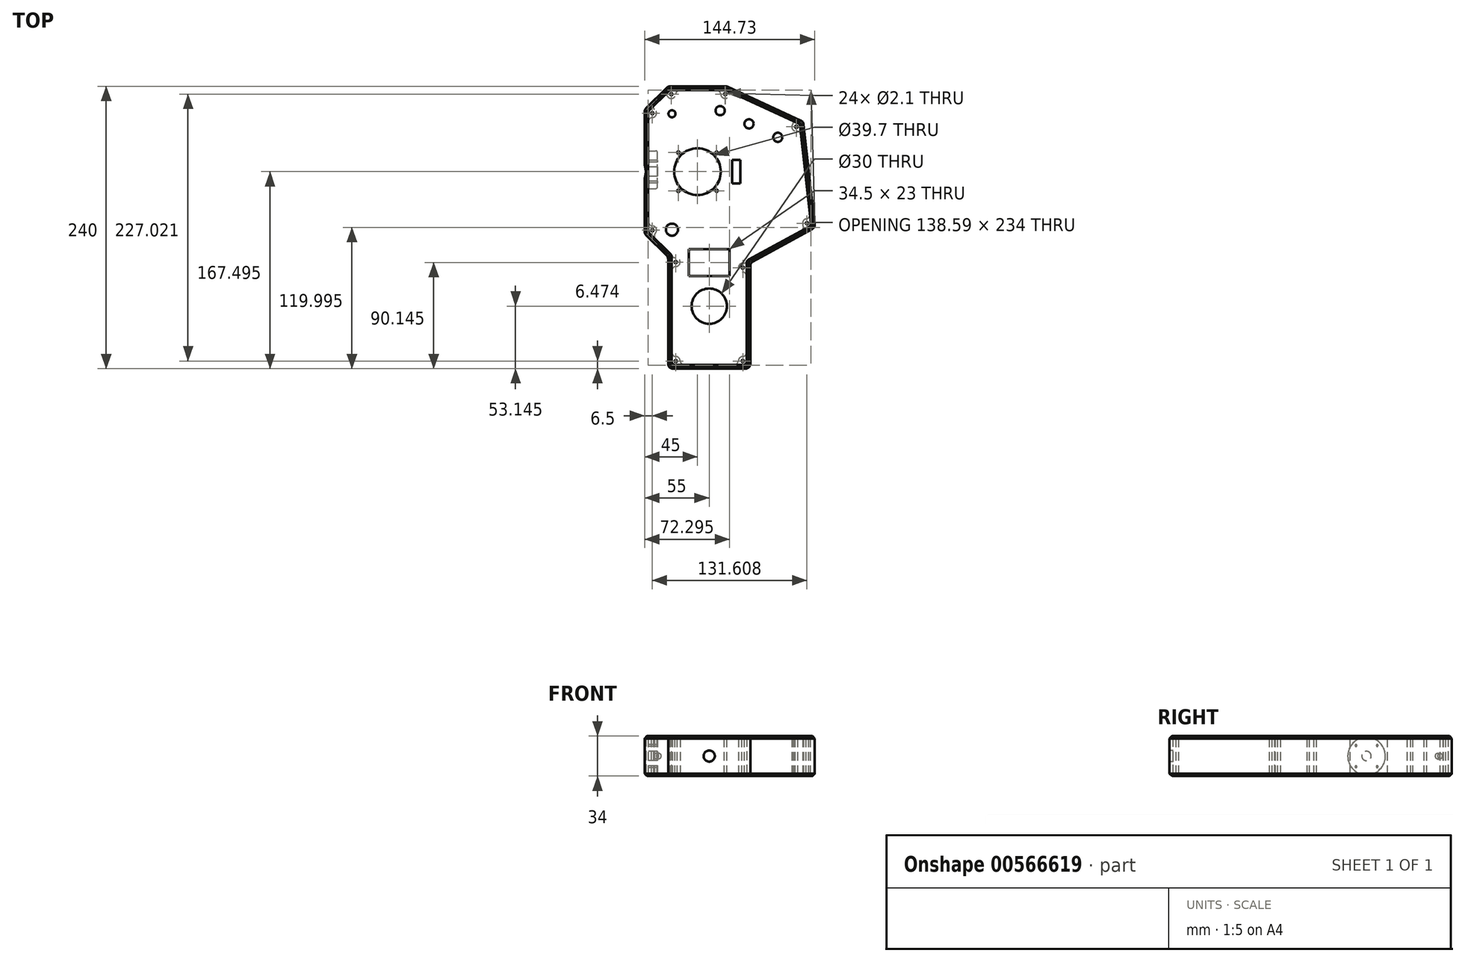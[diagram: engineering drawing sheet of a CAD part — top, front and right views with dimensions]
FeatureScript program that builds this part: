
annotation { "Feature Type Name" : "Feature", "Feature Type Description" : "" }
export const myFeature = defineFeature(function(context is Context, id is Id, definition is map)
    precondition{}
    {
        {
            var Q0;
            Q0=qCreatedBy(makeId("Top.planeOp"),FACE);
            var sketch = newSketch(context, id + "F0", { "sketchPlane" : qUnion([Q0])});
            skLineSegment(sketch, "E0", {"start": v(-64.8, 92.82) * mm, "end": v(-17.33, 92.82) * mm});
            skLineSegment(sketch, "E1", {"start": v(-15.65, 92.45) * mm, "end": v(46.5, 63.76) * mm});
            skLineSegment(sketch, "E2", {"start": v(48.8, 60.57) * mm, "end": v(58.25, -24.52) * mm});
            skLineSegment(sketch, "E3", {"start": v(56.2, -28.47) * mm, "end": v(5.63, -56.05) * mm});
            skLineSegment(sketch, "E4", {"start": v(3.55, -59.56) * mm, "end": v(3.55, -143.18) * mm});
            skLineSegment(sketch, "E5", {"start": v(-0.45, -147.18) * mm, "end": v(-62.45, -147.18) * mm});
            skLineSegment(sketch, "E6", {"start": v(-66.45, -143.18) * mm, "end": v(-66.45, -53.84) * mm});
            skLineSegment(sketch, "E7", {"start": v(-67.62, -51.01) * mm, "end": v(-85.28, -33.36) * mm});
            skLineSegment(sketch, "E8", {"start": v(-86.45, -30.53) * mm, "end": v(-86.45, 71.16) * mm});
            skLineSegment(sketch, "E9", {"start": v(-85.28, 73.99) * mm, "end": v(-67.62, 91.64) * mm});
            skLineSegment(sketch, "E10.0", {"start": v(53.58, -26.48) * mm, "end": v(2.11, -54.55) * mm});
            skLineSegment(sketch, "E10.1", {"start": v(45.94, 59.12) * mm, "end": v(55.12, -23.51) * mm});
            skLineSegment(sketch, "E10.2", {"start": v(0.55, -57.18) * mm, "end": v(0.55, -141.18) * mm});
            skLineSegment(sketch, "E10.3", {"start": v(-16.51, 89.54) * mm, "end": v(44.22, 61.51) * mm});
            skLineSegment(sketch, "E10.4", {"start": v(-63.96, 89.82) * mm, "end": v(-17.77, 89.82) * mm});
            skLineSegment(sketch, "E10.5", {"start": v(-82.57, 72.45) * mm, "end": v(-66.09, 88.94) * mm});
            skLineSegment(sketch, "E10.6", {"start": v(-2.45, -144.18) * mm, "end": v(-60.45, -144.18) * mm});
            skLineSegment(sketch, "E10.7", {"start": v(-63.45, -141.18) * mm, "end": v(-63.45, -52.18) * mm});
            skLineSegment(sketch, "E10.8", {"start": v(-64.33, -50.06) * mm, "end": v(-82.57, -31.82) * mm});
            skLineSegment(sketch, "E10.9", {"start": v(-83.45, -29.7) * mm, "end": v(-83.45, 70.33) * mm});
            skPoint(sketch, "E11.visualSharp", {"position": v(-66.45, 92.82) * mm});
            skArc(sketch, "E11.filletArc", {"start": v(-64.8, 92.82) * mm, "mid": v(-66.32, 92.51) * mm, "end": v(-67.62, 91.64) * mm});
            skPoint(sketch, "E12.visualSharp", {"position": v(-16.45, 92.82) * mm});
            skArc(sketch, "E12.filletArc", {"start": v(-15.65, 92.45) * mm, "mid": v(-16.47, 92.72) * mm, "end": v(-17.33, 92.82) * mm});
            skPoint(sketch, "E13.visualSharp", {"position": v(48.55, 62.82) * mm});
            skArc(sketch, "E13.filletArc", {"start": v(48.8, 60.57) * mm, "mid": v(48.07, 62.47) * mm, "end": v(46.5, 63.76) * mm});
            skPoint(sketch, "E14.visualSharp", {"position": v(58.55, -27.18) * mm});
            skArc(sketch, "E14.filletArc", {"start": v(56.2, -28.47) * mm, "mid": v(57.83, -26.8) * mm, "end": v(58.25, -24.52) * mm});
            skPoint(sketch, "E15.visualSharp", {"position": v(3.55, -57.18) * mm});
            skArc(sketch, "E15.filletArc", {"start": v(5.63, -56.05) * mm, "mid": v(4.11, -57.52) * mm, "end": v(3.55, -59.56) * mm});
            skPoint(sketch, "E16.visualSharp", {"position": v(3.55, -147.18) * mm});
            skArc(sketch, "E16.filletArc", {"start": v(-0.45, -147.18) * mm, "mid": v(2.38, -146.01) * mm, "end": v(3.55, -143.18) * mm});
            skPoint(sketch, "E17.visualSharp", {"position": v(-66.45, -147.18) * mm});
            skArc(sketch, "E17.filletArc", {"start": v(-66.45, -143.18) * mm, "mid": v(-65.28, -146.01) * mm, "end": v(-62.45, -147.18) * mm});
            skPoint(sketch, "E18.visualSharp", {"position": v(-66.45, -52.18) * mm});
            skArc(sketch, "E18.filletArc", {"start": v(-66.45, -53.84) * mm, "mid": v(-66.75, -52.31) * mm, "end": v(-67.62, -51.01) * mm});
            skPoint(sketch, "E19.visualSharp", {"position": v(-86.45, -32.18) * mm});
            skArc(sketch, "E19.filletArc", {"start": v(-86.45, -30.53) * mm, "mid": v(-86.15, -32.06) * mm, "end": v(-85.28, -33.36) * mm});
            skPoint(sketch, "E20.visualSharp", {"position": v(-86.45, 72.82) * mm});
            skArc(sketch, "E20.filletArc", {"start": v(-85.28, 73.99) * mm, "mid": v(-86.15, 72.69) * mm, "end": v(-86.45, 71.16) * mm});
            skPoint(sketch, "E21.visualSharp", {"position": v(-83.45, -30.94) * mm});
            skArc(sketch, "E21.filletArc", {"start": v(-83.45, -29.7) * mm, "mid": v(-83.22, -30.85) * mm, "end": v(-82.57, -31.82) * mm});
            skPoint(sketch, "E22.visualSharp", {"position": v(-83.45, 71.57) * mm});
            skArc(sketch, "E22.filletArc", {"start": v(-82.57, 72.45) * mm, "mid": v(-83.22, 71.48) * mm, "end": v(-83.45, 70.33) * mm});
            skPoint(sketch, "E23.visualSharp", {"position": v(-65.2, 89.82) * mm});
            skArc(sketch, "E23.filletArc", {"start": v(-63.96, 89.82) * mm, "mid": v(-65.11, 89.59) * mm, "end": v(-66.09, 88.94) * mm});
            skPoint(sketch, "E24.visualSharp", {"position": v(-17.1, 89.82) * mm});
            skArc(sketch, "E24.filletArc", {"start": v(-16.51, 89.54) * mm, "mid": v(-17.12, 89.75) * mm, "end": v(-17.77, 89.82) * mm});
            skPoint(sketch, "E25.visualSharp", {"position": v(-63.45, -50.94) * mm});
            skArc(sketch, "E25.filletArc", {"start": v(-63.45, -52.18) * mm, "mid": v(-63.68, -51.04) * mm, "end": v(-64.33, -50.06) * mm});
            skPoint(sketch, "E26.visualSharp", {"position": v(0.55, -55.4) * mm});
            skArc(sketch, "E26.filletArc", {"start": v(2.11, -54.55) * mm, "mid": v(0.97, -55.65) * mm, "end": v(0.55, -57.18) * mm});
            skPoint(sketch, "E27.visualSharp", {"position": v(55.35, -25.52) * mm});
            skArc(sketch, "E27.filletArc", {"start": v(53.58, -26.48) * mm, "mid": v(54.8, -25.23) * mm, "end": v(55.12, -23.51) * mm});
            skPoint(sketch, "E28.visualSharp", {"position": v(45.76, 60.8) * mm});
            skArc(sketch, "E28.filletArc", {"start": v(45.94, 59.12) * mm, "mid": v(45.4, 60.54) * mm, "end": v(44.22, 61.51) * mm});
            skPoint(sketch, "E29.visualSharp", {"position": v(0.55, -144.18) * mm});
            skArc(sketch, "E29.filletArc", {"start": v(-2.45, -144.18) * mm, "mid": v(-0.33, -143.3) * mm, "end": v(0.55, -141.18) * mm});
            skPoint(sketch, "E30.visualSharp", {"position": v(-63.45, -144.18) * mm});
            skArc(sketch, "E30.filletArc", {"start": v(-63.45, -141.18) * mm, "mid": v(-62.57, -143.3) * mm, "end": v(-60.45, -144.18) * mm});
            skSolve(sketch);
        }
        {
            var Q0;
            Q0=makeQuery(id+"F0.imprint","IMPRINT",FACE,{"disambiguationData":[TD([[makeQuery(id+"F0.imprint","IMPRINT",EDGE,{"derivedFrom":sQuery(id+"F0.wireOp",EDGE,"E0")}),-1.0]])]});
            extrude(context, id + "F1", {"entities" : qUnion([Q0]), "endBound" : BoundingType.SYMMETRIC, "depth" : 34 * mm, "offsetDistance" : 25 * mm});
        }
        {
            var Q0;
            Q0=qCreatedBy(makeId("Top.planeOp"),FACE);
            var sketch = newSketch(context, id + "F2", { "sketchPlane" : qUnion([Q0])});
            skLineSegment(sketch, "E31.0", {"start": v(-84.95, -31.56) * mm, "end": v(-84.95, 72.2) * mm, "construction": true});
            skLineSegment(sketch, "E31.1", {"start": v(-64.95, -51.56) * mm, "end": v(-84.95, -31.56) * mm, "construction": true});
            skLineSegment(sketch, "E31.2", {"start": v(-84.95, 72.2) * mm, "end": v(-65.83, 91.32) * mm, "construction": true});
            skLineSegment(sketch, "E31.3", {"start": v(-64.95, -145.68) * mm, "end": v(-64.95, -51.56) * mm, "construction": true});
            skLineSegment(sketch, "E31.4", {"start": v(2.05, -145.68) * mm, "end": v(-64.95, -145.68) * mm, "construction": true});
            skLineSegment(sketch, "E31.5", {"start": v(2.05, -56.3) * mm, "end": v(2.05, -145.68) * mm, "construction": true});
            skLineSegment(sketch, "E31.6", {"start": v(-65.83, 91.32) * mm, "end": v(-16.78, 91.32) * mm, "construction": true});
            skLineSegment(sketch, "E31.7", {"start": v(-16.78, 91.32) * mm, "end": v(47.15, 61.8) * mm, "construction": true});
            skLineSegment(sketch, "E31.8", {"start": v(47.15, 61.8) * mm, "end": v(56.95, -26.35) * mm, "construction": true});
            skLineSegment(sketch, "E31.9", {"start": v(56.95, -26.35) * mm, "end": v(2.05, -56.3) * mm, "construction": true});
            skSolve(sketch);
        }
        {
            var Q0;
            Q0=qCreatedBy(makeId("Top.planeOp"),FACE);
            var sketch = newSketch(context, id + "F3", { "sketchPlane" : qUnion([Q0])});
            skCircle(sketch, "E32", {"center": v(-79.95, 70.12) * mm, "radius": 3.75 * mm});
            skCircle(sketch, "E33", {"center": v(-79.95, 70.12) * mm, "radius": 1.05 * mm});
            skCircle(sketch, "E34", {"center": v(-63.76, 86.32) * mm, "radius": 3.75 * mm});
            skCircle(sketch, "E35", {"center": v(-63.76, 86.32) * mm, "radius": 1.05 * mm});
            skCircle(sketch, "E36", {"center": v(-17.88, 86.32) * mm, "radius": 3.75 * mm});
            skCircle(sketch, "E37", {"center": v(-17.88, 86.32) * mm, "radius": 1.05 * mm});
            skCircle(sketch, "E38", {"center": v(42.5, 58.45) * mm, "radius": 3.75 * mm});
            skCircle(sketch, "E39", {"center": v(42.5, 58.45) * mm, "radius": 1.05 * mm});
            skCircle(sketch, "E40", {"center": v(51.6, -23.57) * mm, "radius": 3.75 * mm});
            skCircle(sketch, "E41", {"center": v(51.6, -23.57) * mm, "radius": 1.05 * mm});
            skCircle(sketch, "E42", {"center": v(-2.95, -140.68) * mm, "radius": 3.75 * mm});
            skCircle(sketch, "E43", {"center": v(-2.95, -140.68) * mm, "radius": 1.05 * mm});
            skCircle(sketch, "E44", {"center": v(-59.95, -140.68) * mm, "radius": 3.75 * mm});
            skCircle(sketch, "E45", {"center": v(-59.95, -140.68) * mm, "radius": 1.05 * mm});
            skCircle(sketch, "E46", {"center": v(-79.95, -29.5) * mm, "radius": 3.75 * mm});
            skCircle(sketch, "E47", {"center": v(-79.95, -29.5) * mm, "radius": 1.05 * mm});
            skCircle(sketch, "E48", {"center": v(-59.95, -56.56) * mm, "radius": 3.75 * mm});
            skCircle(sketch, "E49", {"center": v(-59.95, -56.56) * mm, "radius": 1.05 * mm});
            skCircle(sketch, "E50", {"center": v(-2.95, -61.3) * mm, "radius": 3.75 * mm});
            skCircle(sketch, "E51", {"center": v(-2.95, -61.3) * mm, "radius": 1.05 * mm});
            skLineSegment(sketch, "E52.bottom", {"start": v(-83.45, 5.97) * mm, "end": v(-75.45, 5.97) * mm});
            skLineSegment(sketch, "E52.top", {"start": v(-83.45, 37.97) * mm, "end": v(-75.45, 37.97) * mm});
            skLineSegment(sketch, "E52.left", {"start": v(-83.45, 5.97) * mm, "end": v(-83.45, 37.97) * mm});
            skLineSegment(sketch, "E52.right", {"start": v(-75.45, 5.97) * mm, "end": v(-75.45, 37.97) * mm});
            skSolve(sketch);
        }
        {
            var Q0;
            Q0=makeQuery(id+"F3.imprint","IMPRINT",FACE,{"disambiguationData":[TD([[makeQuery(id+"F3.imprint","IMPRINT",EDGE,{"derivedFrom":sQuery(id+"F3.wireOp",EDGE,"E44")}),1.0]])]});
            var Q1;
            Q1=makeQuery(id+"F3.imprint","IMPRINT",FACE,{"disambiguationData":[TD([[makeQuery(id+"F3.imprint","IMPRINT",EDGE,{"derivedFrom":sQuery(id+"F3.wireOp",EDGE,"E42")}),1.0]])]});
            var Q2;
            Q2=makeQuery(id+"F3.imprint","IMPRINT",FACE,{"disambiguationData":[TD([[makeQuery(id+"F3.imprint","IMPRINT",EDGE,{"derivedFrom":sQuery(id+"F3.wireOp",EDGE,"E50")}),1.0]])]});
            var Q3;
            Q3=makeQuery(id+"F3.imprint","IMPRINT",FACE,{"disambiguationData":[TD([[makeQuery(id+"F3.imprint","IMPRINT",EDGE,{"derivedFrom":sQuery(id+"F3.wireOp",EDGE,"E48")}),1.0]])]});
            var Q4;
            Q4=makeQuery(id+"F3.imprint","IMPRINT",FACE,{"disambiguationData":[TD([[makeQuery(id+"F3.imprint","IMPRINT",EDGE,{"derivedFrom":sQuery(id+"F3.wireOp",EDGE,"E46")}),1.0]])]});
            var Q5;
            Q5=makeQuery(id+"F3.imprint","IMPRINT",FACE,{"disambiguationData":[TD([[makeQuery(id+"F3.imprint","IMPRINT",EDGE,{"derivedFrom":sQuery(id+"F3.wireOp",EDGE,"E40")}),1.0]])]});
            var Q6;
            Q6=makeQuery(id+"F3.imprint","IMPRINT",FACE,{"disambiguationData":[TD([[makeQuery(id+"F3.imprint","IMPRINT",EDGE,{"derivedFrom":sQuery(id+"F3.wireOp",EDGE,"E38")}),1.0]])]});
            var Q7;
            Q7=makeQuery(id+"F3.imprint","IMPRINT",FACE,{"disambiguationData":[TD([[makeQuery(id+"F3.imprint","IMPRINT",EDGE,{"derivedFrom":sQuery(id+"F3.wireOp",EDGE,"E36")}),1.0]])]});
            var Q8;
            Q8=makeQuery(id+"F3.imprint","IMPRINT",FACE,{"disambiguationData":[TD([[makeQuery(id+"F3.imprint","IMPRINT",EDGE,{"derivedFrom":sQuery(id+"F3.wireOp",EDGE,"E34")}),1.0]])]});
            var Q9;
            Q9=makeQuery(id+"F3.imprint","IMPRINT",FACE,{"disambiguationData":[TD([[makeQuery(id+"F3.imprint","IMPRINT",EDGE,{"derivedFrom":sQuery(id+"F3.wireOp",EDGE,"E32")}),1.0]])]});
            var Q10;
            Q10=makeQuery(id+"F3.imprint","IMPRINT",FACE,{"disambiguationData":[TD([[makeQuery(id+"F3.imprint","IMPRINT",EDGE,{"derivedFrom":sQuery(id+"F3.wireOp",EDGE,"E52.bottom")}),1.0]])]});
            extrude(context, id + "F4", {"entities" : qUnion([Q0, Q1, Q2, Q3, Q4, Q5, Q6, Q7, Q8, Q9, Q10]), "operationType" : NewBodyOperationType.ADD, "endBound" : BoundingType.SYMMETRIC, "depth" : 30 * mm, "offsetDistance" : 25 * mm});
        }
        {
            var Q0;
            Q0=makeQuery(id+"F4.boolean.opBoolean","INTERSECT",EDGE,{"disambiguationData":[OD(0.0)],"derivedFrom":[makeQuery(id+"F1.opExtrude","SWEPT_FACE",FACE,{"disambiguationData":[OSD([sQuery(id+"F0.wireOp",EDGE,"E10.7")])]}),makeQuery(id+"F4.opExtrude","SWEPT_FACE",FACE,{"disambiguationData":[OSD([sQuery(id+"F3.wireOp",EDGE,"E48")])]})]});
            var Q1;
            Q1=makeQuery(id+"F4.boolean.opBoolean","INTERSECT",EDGE,{"disambiguationData":[OD(1.0)],"derivedFrom":[makeQuery(id+"F1.opExtrude","SWEPT_FACE",FACE,{"disambiguationData":[OSD([sQuery(id+"F0.wireOp",EDGE,"E10.7")])]}),makeQuery(id+"F4.opExtrude","SWEPT_FACE",FACE,{"disambiguationData":[OSD([sQuery(id+"F3.wireOp",EDGE,"E48")])]})]});
            var Q2;
            Q2=makeQuery(id+"F4.boolean.opBoolean","INTERSECT",EDGE,{"derivedFrom":[makeQuery(id+"F1.opExtrude","SWEPT_FACE",FACE,{"disambiguationData":[OSD([sQuery(id+"F0.wireOp",EDGE,"E10.9")])]}),makeQuery(id+"F4.opExtrude","SWEPT_FACE",FACE,{"disambiguationData":[OSD([sQuery(id+"F3.wireOp",EDGE,"E32")])]})]});
            var Q3;
            Q3=makeQuery(id+"F4.boolean.opBoolean","INTERSECT",EDGE,{"derivedFrom":[makeQuery(id+"F1.opExtrude","SWEPT_FACE",FACE,{"disambiguationData":[OSD([sQuery(id+"F0.wireOp",EDGE,"E10.4")])]}),makeQuery(id+"F4.opExtrude","SWEPT_FACE",FACE,{"disambiguationData":[OSD([sQuery(id+"F3.wireOp",EDGE,"E36")])]})]});
            var Q4;
            Q4=makeQuery(id+"F4.boolean.opBoolean","INTERSECT",EDGE,{"derivedFrom":[makeQuery(id+"F1.opExtrude","SWEPT_FACE",FACE,{"disambiguationData":[OSD([sQuery(id+"F0.wireOp",EDGE,"E10.4")])]}),makeQuery(id+"F4.opExtrude","SWEPT_FACE",FACE,{"disambiguationData":[OSD([sQuery(id+"F3.wireOp",EDGE,"E34")])]})]});
            var Q5;
            Q5=makeQuery(id+"F4.boolean.opBoolean","INTERSECT",EDGE,{"derivedFrom":[makeQuery(id+"F1.opExtrude","SWEPT_FACE",FACE,{"disambiguationData":[OSD([sQuery(id+"F0.wireOp",EDGE,"E10.1")])]}),makeQuery(id+"F4.opExtrude","SWEPT_FACE",FACE,{"disambiguationData":[OSD([sQuery(id+"F3.wireOp",EDGE,"E38")])]})]});
            var Q6;
            Q6=makeQuery(id+"F4.boolean.opBoolean","INTERSECT",EDGE,{"derivedFrom":[makeQuery(id+"F1.opExtrude","SWEPT_FACE",FACE,{"disambiguationData":[OSD([sQuery(id+"F0.wireOp",EDGE,"E10.0")])]}),makeQuery(id+"F4.opExtrude","SWEPT_FACE",FACE,{"disambiguationData":[OSD([sQuery(id+"F3.wireOp",EDGE,"E40")])]})]});
            var Q7;
            Q7=makeQuery(id+"F4.boolean.opBoolean","INTERSECT",EDGE,{"derivedFrom":[makeQuery(id+"F1.opExtrude","SWEPT_FACE",FACE,{"disambiguationData":[OSD([sQuery(id+"F0.wireOp",EDGE,"E10.1")])]}),makeQuery(id+"F4.opExtrude","SWEPT_FACE",FACE,{"disambiguationData":[OSD([sQuery(id+"F3.wireOp",EDGE,"E40")])]})]});
            var Q8;
            Q8=makeQuery(id+"F4.boolean.opBoolean","INTERSECT",EDGE,{"derivedFrom":[makeQuery(id+"F1.opExtrude","SWEPT_FACE",FACE,{"disambiguationData":[OSD([sQuery(id+"F0.wireOp",EDGE,"E10.8")])]}),makeQuery(id+"F4.opExtrude","SWEPT_FACE",FACE,{"disambiguationData":[OSD([sQuery(id+"F3.wireOp",EDGE,"E46")])]})]});
            var Q9;
            Q9=makeQuery(id+"F4.boolean.opBoolean","INTERSECT",EDGE,{"derivedFrom":[makeQuery(id+"F1.opExtrude","SWEPT_FACE",FACE,{"disambiguationData":[OSD([sQuery(id+"F0.wireOp",EDGE,"E10.9")])]}),makeQuery(id+"F4.opExtrude","SWEPT_FACE",FACE,{"disambiguationData":[OSD([sQuery(id+"F3.wireOp",EDGE,"E46")])]})]});
            var Q10;
            Q10=makeQuery(id+"F4.boolean.opBoolean","INTERSECT",EDGE,{"derivedFrom":[makeQuery(id+"F1.opExtrude","SWEPT_FACE",FACE,{"disambiguationData":[OSD([sQuery(id+"F0.wireOp",EDGE,"E10.7")])]}),makeQuery(id+"F4.opExtrude","SWEPT_FACE",FACE,{"disambiguationData":[OSD([sQuery(id+"F3.wireOp",EDGE,"E44")])]})]});
            var Q11;
            Q11=makeQuery(id+"F4.boolean.opBoolean","INTERSECT",EDGE,{"derivedFrom":[makeQuery(id+"F1.opExtrude","SWEPT_FACE",FACE,{"disambiguationData":[OSD([sQuery(id+"F0.wireOp",EDGE,"E10.6")])]}),makeQuery(id+"F4.opExtrude","SWEPT_FACE",FACE,{"disambiguationData":[OSD([sQuery(id+"F3.wireOp",EDGE,"E44")])]})]});
            var Q12;
            Q12=makeQuery(id+"F4.boolean.opBoolean","INTERSECT",EDGE,{"derivedFrom":[makeQuery(id+"F1.opExtrude","SWEPT_FACE",FACE,{"disambiguationData":[OSD([sQuery(id+"F0.wireOp",EDGE,"E10.6")])]}),makeQuery(id+"F4.opExtrude","SWEPT_FACE",FACE,{"disambiguationData":[OSD([sQuery(id+"F3.wireOp",EDGE,"E42")])]})]});
            var Q13;
            Q13=makeQuery(id+"F4.boolean.opBoolean","INTERSECT",EDGE,{"derivedFrom":[makeQuery(id+"F1.opExtrude","SWEPT_FACE",FACE,{"disambiguationData":[OSD([sQuery(id+"F0.wireOp",EDGE,"E10.2")])]}),makeQuery(id+"F4.opExtrude","SWEPT_FACE",FACE,{"disambiguationData":[OSD([sQuery(id+"F3.wireOp",EDGE,"E42")])]})]});
            var Q14;
            Q14=makeQuery(id+"F4.boolean.opBoolean","INTERSECT",EDGE,{"disambiguationData":[OD(0.0)],"derivedFrom":[makeQuery(id+"F1.opExtrude","SWEPT_FACE",FACE,{"disambiguationData":[OSD([sQuery(id+"F0.wireOp",EDGE,"E10.2")])]}),makeQuery(id+"F4.opExtrude","SWEPT_FACE",FACE,{"disambiguationData":[OSD([sQuery(id+"F3.wireOp",EDGE,"E50")])]})]});
            var Q15;
            Q15=makeQuery(id+"F4.boolean.opBoolean","INTERSECT",EDGE,{"disambiguationData":[OD(1.0)],"derivedFrom":[makeQuery(id+"F1.opExtrude","SWEPT_FACE",FACE,{"disambiguationData":[OSD([sQuery(id+"F0.wireOp",EDGE,"E10.2")])]}),makeQuery(id+"F4.opExtrude","SWEPT_FACE",FACE,{"disambiguationData":[OSD([sQuery(id+"F3.wireOp",EDGE,"E50")])]})]});
            var Q16;
            Q16=makeQuery(id+"F4.opExtrude","SWEPT_EDGE",EDGE,{"disambiguationData":[OSD([sQuery(id+"F3.wireOp",EDGE,"E52.bottom"),sQuery(id+"F3.wireOp",EDGE,"E52.left")])]});
            var Q17;
            Q17=makeQuery(id+"F4.opExtrude","SWEPT_EDGE",EDGE,{"disambiguationData":[OSD([sQuery(id+"F3.wireOp",EDGE,"E52.top"),sQuery(id+"F3.wireOp",EDGE,"E52.left")])]});
            fillet(context, id + "F5", {"entities" : qUnion([Q0, Q1, Q2, Q3, Q4, Q5, Q6, Q7, Q8, Q9, Q10, Q11, Q12, Q13, Q14, Q15, Q16, Q17]), "radius" : 4 * mm, "tangentPropagation" : true, "defaultsChanged" : false, "vertexSettings" : [], "allowEdgeOverflow" : false});
        }
        {
            var Q0;
            Q0=makeQuery(id+"F1.opExtrude","SWEPT_FACE",FACE,{"disambiguationData":[OSD([sQuery(id+"F0.wireOp",EDGE,"E5")])]});
            var sketch = newSketch(context, id + "F6", { "sketchPlane" : qUnion([Q0])});
            skCircle(sketch, "E53", {"center": v(-31.45, 0) * mm, "radius": 4.75 * mm});
            skSolve(sketch);
        }
        {
            var Q0;
            Q0=makeQuery(id+"F6.imprint","IMPRINT",FACE,{"disambiguationData":[TD([[makeQuery(id+"F6.imprint","IMPRINT",EDGE,{"derivedFrom":sQuery(id+"F6.wireOp",EDGE,"E53")}),1.0]])]});
            var Q1;
            Q1=makeQuery(id+"F6.imprint","IMPRINT",FACE,{"disambiguationData":[TD([[makeQuery(id+"F6.imprint","IMPRINT",EDGE,{"derivedFrom":sQuery(id+"F6.wireOp",EDGE,"O80JE7wC-Ytc9-j5uM-N2nM-kXgGOOiKGs8d")}),1.0]])]});
            extrude(context, id + "F7", {"entities" : qUnion([Q0, Q1]), "operationType" : NewBodyOperationType.REMOVE, "oppositeDirection" : true, "depth" : 3 * mm, "offsetDistance" : 25 * mm});
        }
        {
            var Q0;
            Q0=makeQuery(id+"F1.opExtrude","SWEPT_FACE",FACE,{"disambiguationData":[OSD([sQuery(id+"F0.wireOp",EDGE,"E8")])]});
            var sketch = newSketch(context, id + "F8", { "sketchPlane" : qUnion([Q0])});
            skCircle(sketch, "E54", {"center": v(-20.32, 0) * mm, "radius": 16 * mm});
            skSolve(sketch);
        }
        {
            var Q0;
            {var subQ0=sQuery(id+"F8.wireOp",EDGE,"E54");var subQ1=sQuery(id+"F0.wireOp",EDGE,"E8");var subQ2=makeQuery(id+"F1.opExtrude","CAP_EDGE",EDGE,{"disambiguationData":[OSD([subQ1])],"isStart":false});var subQ3=makeQuery(id+"F8.imprint","INTERSECT",VERTEX,{"disambiguationData":[OD(0.0)],"derivedFrom":[subQ2,subQ0]});Q0=makeQuery(id+"F8.imprint","IMPRINT",FACE,{"disambiguationData":[TD([[makeQuery(id+"F8.imprint","IMPRINT",EDGE,{"disambiguationData":[TD([[subQ3,-1.0]])],"derivedFrom":subQ0}),1.0]])]});}
            extrude(context, id + "F9", {"entities" : qUnion([Q0]), "operationType" : NewBodyOperationType.REMOVE, "oppositeDirection" : true, "depth" : 1 * mm, "offsetDistance" : 25 * mm});
        }
        {
            var Q0;
            Q0=makeQuery(id+"F9.boolean.opBoolean","COPY",FACE,{"derivedFrom":makeQuery(id+"F9.opExtrude","CAP_FACE",FACE,{"disambiguationData":[OSD([sQuery(id+"F0.wireOp",EDGE,"E8"),sQuery(id+"F8.wireOp",EDGE,"E54")])],"isStart":false})});
            var sketch = newSketch(context, id + "F10", { "sketchPlane" : qUnion([Q0])});
            skCircle(sketch, "E55", {"center": v(-20.32, 0) * mm, "radius": 4 * mm});
            skCircle(sketch, "E56", {"center": v(-29.32, 9) * mm, "radius": 0.8 * mm});
            skCircle(sketch, "E57", {"center": v(-11.32, 9) * mm, "radius": 0.8 * mm});
            skCircle(sketch, "E58", {"center": v(-11.32, -9) * mm, "radius": 0.8 * mm});
            skCircle(sketch, "E59", {"center": v(-29.32, -9) * mm, "radius": 0.8 * mm});
            skSolve(sketch);
        }
        {
            var Q0;
            Q0=makeQuery(id+"F10.imprint","IMPRINT",FACE,{"disambiguationData":[TD([[makeQuery(id+"F10.imprint","IMPRINT",EDGE,{"derivedFrom":sQuery(id+"F10.wireOp",EDGE,"E56")}),1.0]])]});
            var Q1;
            Q1=makeQuery(id+"F10.imprint","IMPRINT",FACE,{"disambiguationData":[TD([[makeQuery(id+"F10.imprint","IMPRINT",EDGE,{"derivedFrom":sQuery(id+"F10.wireOp",EDGE,"E57")}),1.0]])]});
            var Q2;
            Q2=makeQuery(id+"F10.imprint","IMPRINT",FACE,{"disambiguationData":[TD([[makeQuery(id+"F10.imprint","IMPRINT",EDGE,{"derivedFrom":sQuery(id+"F10.wireOp",EDGE,"E55")}),1.0]])]});
            var Q3;
            Q3=makeQuery(id+"F10.imprint","IMPRINT",FACE,{"disambiguationData":[TD([[makeQuery(id+"F10.imprint","IMPRINT",EDGE,{"derivedFrom":sQuery(id+"F10.wireOp",EDGE,"E58")}),1.0]])]});
            var Q4;
            Q4=makeQuery(id+"F10.imprint","IMPRINT",FACE,{"disambiguationData":[TD([[makeQuery(id+"F10.imprint","IMPRINT",EDGE,{"derivedFrom":sQuery(id+"F10.wireOp",EDGE,"E59")}),1.0]])]});
            extrude(context, id + "F11", {"entities" : qUnion([Q0, Q1, Q2, Q3, Q4]), "operationType" : NewBodyOperationType.REMOVE, "depth" : -10.9 * mm, "offsetDistance" : 25 * mm});
        }
        {
            var Q0;
            Q0=makeQuery(id+"F4.opExtrude","SWEPT_EDGE",EDGE,{"disambiguationData":[OSD([sQuery(id+"F3.wireOp",EDGE,"E52.bottom"),sQuery(id+"F3.wireOp",EDGE,"E52.right")])]});
            var Q1;
            Q1=makeQuery(id+"F4.opExtrude","SWEPT_EDGE",EDGE,{"disambiguationData":[OSD([sQuery(id+"F3.wireOp",EDGE,"E52.top"),sQuery(id+"F3.wireOp",EDGE,"E52.right")])]});
            fillet(context, id + "F12", {"entities" : qUnion([Q0, Q1]), "radius" : 1.5 * mm, "tangentPropagation" : true, "allowEdgeOverflow" : false});
        }
        {
            var Q0;
            Q0=makeQuery(id+"F1.opExtrude","SWEPT_FACE",FACE,{"disambiguationData":[OSD([sQuery(id+"F0.wireOp",EDGE,"E9")])]});
            var sketch = newSketch(context, id + "F13", { "sketchPlane" : qUnion([Q0])});
            skCircle(sketch, "E60", {"center": v(-4.5, 0) * mm, "radius": 2.5 * mm});
            skPoint(sketch, "E60.centerSnap0", {"position": v(-4.5, 17) * mm});
            skSolve(sketch);
        }
        {
            var Q0;
            Q0=makeQuery(id+"F13.imprint","IMPRINT",FACE,{"disambiguationData":[TD([[makeQuery(id+"F13.imprint","IMPRINT",EDGE,{"derivedFrom":sQuery(id+"F13.wireOp",EDGE,"E60")}),1.0]])]});
            extrude(context, id + "F14", {"entities" : qUnion([Q0]), "operationType" : NewBodyOperationType.REMOVE, "oppositeDirection" : true, "depth" : 3 * mm, "offsetDistance" : 25 * mm});
        }
        {
            var Q0;
            Q0=makeQuery(id+"F4.boolean.opBoolean","INTERSECT",EDGE,{"derivedFrom":[makeQuery(id+"F1.opExtrude","SWEPT_FACE",FACE,{"disambiguationData":[OSD([sQuery(id+"F0.wireOp",EDGE,"E10.5")])]}),makeQuery(id+"F4.opExtrude","SWEPT_FACE",FACE,{"disambiguationData":[OSD([sQuery(id+"F3.wireOp",EDGE,"E34")])]})]});
            var Q1;
            Q1=makeQuery(id+"F4.boolean.opBoolean","INTERSECT",EDGE,{"derivedFrom":[makeQuery(id+"F1.opExtrude","SWEPT_FACE",FACE,{"disambiguationData":[OSD([sQuery(id+"F0.wireOp",EDGE,"E10.5")])]}),makeQuery(id+"F4.opExtrude","SWEPT_FACE",FACE,{"disambiguationData":[OSD([sQuery(id+"F3.wireOp",EDGE,"E32")])]})]});
            var Q2;
            Q2=makeQuery(id+"F4.boolean.opBoolean","INTERSECT",EDGE,{"derivedFrom":[makeQuery(id+"F1.opExtrude","SWEPT_FACE",FACE,{"disambiguationData":[OSD([sQuery(id+"F0.wireOp",EDGE,"E10.3")])]}),makeQuery(id+"F4.opExtrude","SWEPT_FACE",FACE,{"disambiguationData":[OSD([sQuery(id+"F3.wireOp",EDGE,"E38")])]})]});
            var Q3;
            Q3=makeQuery(id+"F4.boolean.opBoolean","INTERSECT",EDGE,{"derivedFrom":[makeQuery(id+"F1.opExtrude","SWEPT_FACE",FACE,{"disambiguationData":[OSD([sQuery(id+"F0.wireOp",EDGE,"E10.3")])]}),makeQuery(id+"F4.opExtrude","SWEPT_FACE",FACE,{"disambiguationData":[OSD([sQuery(id+"F3.wireOp",EDGE,"E36")])]})]});
            fillet(context, id + "F15", {"entities" : qUnion([Q0, Q1, Q2, Q3]), "radius" : 2 * mm, "tangentPropagation" : true, "allowEdgeOverflow" : false});
        }
        {
            var Q0;
            Q0=makeQuery(id+"F1.opExtrude","CAP_FACE",FACE,{"disambiguationData":[OSD([sQuery(id+"F0.wireOp",EDGE,"E0"),sQuery(id+"F0.wireOp",EDGE,"E1"),sQuery(id+"F0.wireOp",EDGE,"E2"),sQuery(id+"F0.wireOp",EDGE,"E3"),sQuery(id+"F0.wireOp",EDGE,"E4"),sQuery(id+"F0.wireOp",EDGE,"E5"),sQuery(id+"F0.wireOp",EDGE,"E6"),sQuery(id+"F0.wireOp",EDGE,"E7"),sQuery(id+"F0.wireOp",EDGE,"E8"),sQuery(id+"F0.wireOp",EDGE,"E9"),sQuery(id+"F0.wireOp",EDGE,"E10.0"),sQuery(id+"F0.wireOp",EDGE,"E10.1"),sQuery(id+"F0.wireOp",EDGE,"E10.2"),sQuery(id+"F0.wireOp",EDGE,"E10.3"),sQuery(id+"F0.wireOp",EDGE,"E10.4"),sQuery(id+"F0.wireOp",EDGE,"E10.5"),sQuery(id+"F0.wireOp",EDGE,"E10.6"),sQuery(id+"F0.wireOp",EDGE,"E10.7"),sQuery(id+"F0.wireOp",EDGE,"E10.8"),sQuery(id+"F0.wireOp",EDGE,"E10.9"),sQuery(id+"F0.wireOp",EDGE,"E11.filletArc"),sQuery(id+"F0.wireOp",EDGE,"E12.filletArc"),sQuery(id+"F0.wireOp",EDGE,"E13.filletArc"),sQuery(id+"F0.wireOp",EDGE,"E14.filletArc"),sQuery(id+"F0.wireOp",EDGE,"E15.filletArc"),sQuery(id+"F0.wireOp",EDGE,"E16.filletArc"),sQuery(id+"F0.wireOp",EDGE,"E17.filletArc"),sQuery(id+"F0.wireOp",EDGE,"E18.filletArc"),sQuery(id+"F0.wireOp",EDGE,"E19.filletArc"),sQuery(id+"F0.wireOp",EDGE,"E20.filletArc"),sQuery(id+"F0.wireOp",EDGE,"E21.filletArc"),sQuery(id+"F0.wireOp",EDGE,"E22.filletArc"),sQuery(id+"F0.wireOp",EDGE,"E23.filletArc"),sQuery(id+"F0.wireOp",EDGE,"E24.filletArc"),sQuery(id+"F0.wireOp",EDGE,"E25.filletArc"),sQuery(id+"F0.wireOp",EDGE,"E26.filletArc"),sQuery(id+"F0.wireOp",EDGE,"E27.filletArc"),sQuery(id+"F0.wireOp",EDGE,"E28.filletArc"),sQuery(id+"F0.wireOp",EDGE,"E29.filletArc"),sQuery(id+"F0.wireOp",EDGE,"E30.filletArc")])],"isStart":false});
            var sketch = newSketch(context, id + "F16", { "sketchPlane" : qUnion([Q0])});
            skLineSegment(sketch, "E61.0", {"start": v(-63.96, 89.82) * mm, "end": v(-17.77, 89.82) * mm});
            skLineSegment(sketch, "E61.1", {"start": v(-16.51, 89.54) * mm, "end": v(44.22, 61.51) * mm});
            skLineSegment(sketch, "E61.2", {"start": v(45.94, 59.12) * mm, "end": v(55.12, -23.51) * mm});
            skLineSegment(sketch, "E61.3", {"start": v(53.58, -26.48) * mm, "end": v(2.11, -54.55) * mm});
            skLineSegment(sketch, "E61.4", {"start": v(0.55, -57.18) * mm, "end": v(0.55, -141.18) * mm});
            skLineSegment(sketch, "E61.5", {"start": v(-2.45, -144.18) * mm, "end": v(-60.45, -144.18) * mm});
            skLineSegment(sketch, "E61.6", {"start": v(-63.45, -141.18) * mm, "end": v(-63.45, -52.18) * mm});
            skLineSegment(sketch, "E61.7", {"start": v(-64.33, -50.06) * mm, "end": v(-82.57, -31.82) * mm});
            skLineSegment(sketch, "E61.8", {"start": v(-83.45, -29.7) * mm, "end": v(-83.45, 70.33) * mm});
            skLineSegment(sketch, "E61.9", {"start": v(-82.57, 72.45) * mm, "end": v(-66.09, 88.94) * mm});
            skArc(sketch, "E61.10", {"start": v(-63.96, 89.82) * mm, "mid": v(-65.11, 89.59) * mm, "end": v(-66.09, 88.94) * mm});
            skArc(sketch, "E61.11", {"start": v(-16.51, 89.54) * mm, "mid": v(-17.12, 89.75) * mm, "end": v(-17.77, 89.82) * mm});
            skArc(sketch, "E61.12", {"start": v(-82.57, 72.45) * mm, "mid": v(-83.22, 71.48) * mm, "end": v(-83.45, 70.33) * mm});
            skArc(sketch, "E61.13", {"start": v(-83.45, -29.7) * mm, "mid": v(-83.22, -30.85) * mm, "end": v(-82.57, -31.82) * mm});
            skArc(sketch, "E61.14", {"start": v(-63.45, -52.18) * mm, "mid": v(-63.68, -51.04) * mm, "end": v(-64.33, -50.06) * mm});
            skArc(sketch, "E61.15", {"start": v(45.94, 59.12) * mm, "mid": v(45.4, 60.54) * mm, "end": v(44.22, 61.51) * mm});
            skArc(sketch, "E61.16", {"start": v(53.58, -26.48) * mm, "mid": v(54.8, -25.23) * mm, "end": v(55.12, -23.51) * mm});
            skArc(sketch, "E61.17", {"start": v(2.11, -54.55) * mm, "mid": v(0.97, -55.65) * mm, "end": v(0.55, -57.18) * mm});
            skArc(sketch, "E61.18", {"start": v(-63.45, -141.18) * mm, "mid": v(-62.57, -143.3) * mm, "end": v(-60.45, -144.18) * mm});
            skArc(sketch, "E61.19", {"start": v(-2.45, -144.18) * mm, "mid": v(-0.33, -143.3) * mm, "end": v(0.55, -141.18) * mm});
            skLineSegment(sketch, "E62.0", {"start": v(-64.22, -49.96) * mm, "end": v(-82.42, -31.76) * mm});
            skLineSegment(sketch, "E62.1", {"start": v(45.8, 59.02) * mm, "end": v(54.96, -23.43) * mm});
            skLineSegment(sketch, "E62.2", {"start": v(-16.54, 89.39) * mm, "end": v(44.08, 61.4) * mm});
            skLineSegment(sketch, "E62.3", {"start": v(-63.9, 89.67) * mm, "end": v(-17.8, 89.67) * mm});
            skLineSegment(sketch, "E62.4", {"start": v(-82.42, 72.39) * mm, "end": v(-66.02, 88.79) * mm});
            skLineSegment(sketch, "E62.5", {"start": v(53.42, -26.4) * mm, "end": v(2.04, -54.42) * mm});
            skLineSegment(sketch, "E62.6", {"start": v(-83.3, -29.64) * mm, "end": v(-83.3, 70.27) * mm});
            skArc(sketch, "E62.7", {"start": v(2.04, -54.42) * mm, "mid": v(0.84, -55.58) * mm, "end": v(0.4, -57.18) * mm});
            skLineSegment(sketch, "E62.8", {"start": v(0.4, -57.18) * mm, "end": v(0.4, -141.03) * mm});
            skLineSegment(sketch, "E62.9", {"start": v(-2.6, -144.03) * mm, "end": v(-60.3, -144.03) * mm});
            skLineSegment(sketch, "E62.10", {"start": v(-63.3, -141.03) * mm, "end": v(-63.3, -52.18) * mm});
            skArc(sketch, "E62.11", {"start": v(-63.3, -52.18) * mm, "mid": v(-63.54, -50.98) * mm, "end": v(-64.22, -49.96) * mm});
            skPoint(sketch, "E63.visualSharp", {"position": v(-83.3, 71.51) * mm});
            skArc(sketch, "E63.filletArc", {"start": v(-82.42, 72.39) * mm, "mid": v(-83.07, 71.42) * mm, "end": v(-83.3, 70.27) * mm});
            skPoint(sketch, "E64.visualSharp", {"position": v(-65.14, 89.67) * mm});
            skArc(sketch, "E64.filletArc", {"start": v(-63.9, 89.67) * mm, "mid": v(-65.05, 89.44) * mm, "end": v(-66.02, 88.79) * mm});
            skPoint(sketch, "E65.visualSharp", {"position": v(-17.14, 89.67) * mm});
            skArc(sketch, "E65.filletArc", {"start": v(-16.54, 89.39) * mm, "mid": v(-17.16, 89.6) * mm, "end": v(-17.8, 89.67) * mm});
            skPoint(sketch, "E66.visualSharp", {"position": v(45.62, 60.7) * mm});
            skArc(sketch, "E66.filletArc", {"start": v(45.8, 59.02) * mm, "mid": v(45.26, 60.44) * mm, "end": v(44.08, 61.4) * mm});
            skPoint(sketch, "E67.visualSharp", {"position": v(55.19, -25.43) * mm});
            skArc(sketch, "E67.filletArc", {"start": v(53.42, -26.4) * mm, "mid": v(54.64, -25.15) * mm, "end": v(54.96, -23.43) * mm});
            skPoint(sketch, "E68.visualSharp", {"position": v(0.4, -144.03) * mm});
            skArc(sketch, "E68.filletArc", {"start": v(-2.6, -144.03) * mm, "mid": v(-0.48, -143.16) * mm, "end": v(0.4, -141.03) * mm});
            skPoint(sketch, "E69.visualSharp", {"position": v(-63.3, -144.03) * mm});
            skArc(sketch, "E69.filletArc", {"start": v(-63.3, -141.03) * mm, "mid": v(-62.42, -143.16) * mm, "end": v(-60.3, -144.03) * mm});
            skPoint(sketch, "E70.visualSharp", {"position": v(-83.3, -30.88) * mm});
            skArc(sketch, "E70.filletArc", {"start": v(-83.3, -29.64) * mm, "mid": v(-83.07, -30.79) * mm, "end": v(-82.42, -31.76) * mm});
            skSolve(sketch);
        }
        {
            var Q0;
            Q0=makeQuery(id+"F16.imprint","IMPRINT",FACE,{"disambiguationData":[TD([[makeQuery(id+"F16.imprint","IMPRINT",EDGE,{"derivedFrom":sQuery(id+"F16.wireOp",EDGE,"E62.0")}),-1.0]])]});
            extrude(context, id + "F17", {"entities" : qUnion([Q0]), "depth" : -2 * mm, "offsetDistance" : 25 * mm});
        }
        {
            var Q0;
            Q0=makeQuery(id+"F1.opExtrude","CAP_EDGE",EDGE,{"disambiguationData":[OSD([sQuery(id+"F0.wireOp",EDGE,"E8")])],"isStart":false});
            chamfer(context, id + "F18", {"entities" : qUnion([Q0]), "width" : 2 * mm, "tangentPropagation" : true});
        }
        {
            var Q0;
            Q0=makeQuery(id+"F1.opExtrude","CAP_EDGE",EDGE,{"disambiguationData":[OSD([sQuery(id+"F0.wireOp",EDGE,"E8")])],"isStart":true});
            chamfer(context, id + "F19", {"entities" : qUnion([Q0]), "width" : 2 * mm, "tangentPropagation" : true});
        }
        {
            var Q0;
            Q0=makeQuery(id+"F17.opExtrude","CAP_FACE",FACE,{"disambiguationData":[OSD([sQuery(id+"F16.wireOp",EDGE,"E62.0"),sQuery(id+"F16.wireOp",EDGE,"E62.1"),sQuery(id+"F16.wireOp",EDGE,"E62.2"),sQuery(id+"F16.wireOp",EDGE,"E62.3"),sQuery(id+"F16.wireOp",EDGE,"E62.4"),sQuery(id+"F16.wireOp",EDGE,"E62.5"),sQuery(id+"F16.wireOp",EDGE,"E62.6"),sQuery(id+"F16.wireOp",EDGE,"E62.7"),sQuery(id+"F16.wireOp",EDGE,"E62.8"),sQuery(id+"F16.wireOp",EDGE,"E62.9"),sQuery(id+"F16.wireOp",EDGE,"E62.10"),sQuery(id+"F16.wireOp",EDGE,"E62.11"),sQuery(id+"F16.wireOp",EDGE,"E63.filletArc"),sQuery(id+"F16.wireOp",EDGE,"E64.filletArc"),sQuery(id+"F16.wireOp",EDGE,"E65.filletArc"),sQuery(id+"F16.wireOp",EDGE,"E66.filletArc"),sQuery(id+"F16.wireOp",EDGE,"E67.filletArc"),sQuery(id+"F16.wireOp",EDGE,"E68.filletArc"),sQuery(id+"F16.wireOp",EDGE,"E69.filletArc"),sQuery(id+"F16.wireOp",EDGE,"E70.filletArc")])],"isStart":true});
            var sketch = newSketch(context, id + "F20", { "sketchPlane" : qUnion([Q0])});
            skCircle(sketch, "E71", {"center": v(-41.45, 20.32) * mm, "radius": 19.85 * mm});
            skCircle(sketch, "E72", {"center": v(-63.16, 69.53) * mm, "radius": 3 * mm});
            skCircle(sketch, "E73", {"center": v(-22.2, 72.18) * mm, "radius": 3.9 * mm});
            skCircle(sketch, "E74", {"center": v(26.83, 49.55) * mm, "radius": 3.9 * mm});
            skCircle(sketch, "E75", {"center": v(2.38, 61) * mm, "radius": 3.9 * mm});
            skCircle(sketch, "E76", {"center": v(-63.15, -28.98) * mm, "radius": 5.15 * mm});
            skCircle(sketch, "E77", {"center": v(-31.45, -94.03) * mm, "radius": 15 * mm});
            skLineSegment(sketch, "E78.bottom", {"start": v(-14.2, -45.53) * mm, "end": v(-48.7, -45.53) * mm});
            skLineSegment(sketch, "E78.top", {"start": v(-14.2, -68.53) * mm, "end": v(-48.7, -68.53) * mm});
            skLineSegment(sketch, "E78.left", {"start": v(-14.2, -45.53) * mm, "end": v(-14.2, -68.53) * mm});
            skLineSegment(sketch, "E78.right", {"start": v(-48.7, -45.53) * mm, "end": v(-48.7, -68.53) * mm});
            skPoint(sketch, "E78.middle", {"position": v(-31.45, -57.03) * mm});
            skLineSegment(sketch, "E79.bottom", {"start": v(-4.95, 30.32) * mm, "end": v(-11.95, 30.32) * mm});
            skLineSegment(sketch, "E79.top", {"start": v(-4.95, 10.32) * mm, "end": v(-11.95, 10.32) * mm});
            skLineSegment(sketch, "E79.left", {"start": v(-4.95, 30.32) * mm, "end": v(-4.95, 10.32) * mm});
            skLineSegment(sketch, "E79.right", {"start": v(-11.95, 30.32) * mm, "end": v(-11.95, 10.32) * mm});
            skPoint(sketch, "E79.middle", {"position": v(-8.45, 20.32) * mm});
            skCircle(sketch, "E80", {"center": v(-57.7, 36.57) * mm, "radius": 1.05 * mm});
            skCircle(sketch, "E81", {"center": v(-25.2, 36.57) * mm, "radius": 1.05 * mm});
            skCircle(sketch, "E82", {"center": v(-25.2, 4.07) * mm, "radius": 1.05 * mm});
            skCircle(sketch, "E83", {"center": v(-57.7, 4.07) * mm, "radius": 1.05 * mm});
            skCircle(sketch, "E84", {"center": v(-79.9, 70.1) * mm, "radius": 1.05 * mm});
            skCircle(sketch, "E85", {"center": v(-63.7, 86.3) * mm, "radius": 1.05 * mm});
            skCircle(sketch, "E86", {"center": v(-17.83, 86.3) * mm, "radius": 1.05 * mm});
            skCircle(sketch, "E87", {"center": v(42.55, 58.43) * mm, "radius": 1.05 * mm});
            skCircle(sketch, "E88", {"center": v(51.66, -23.59) * mm, "radius": 1.05 * mm});
            skCircle(sketch, "E89", {"center": v(-2.9, -140.7) * mm, "radius": 1.05 * mm});
            skCircle(sketch, "E90", {"center": v(-59.9, -140.7) * mm, "radius": 1.05 * mm});
            skCircle(sketch, "E91", {"center": v(-79.9, -29.51) * mm, "radius": 1.05 * mm});
            skCircle(sketch, "E92", {"center": v(-59.95, -56.56) * mm, "radius": 1.05 * mm});
            skCircle(sketch, "E93", {"center": v(-2.9, -61.32) * mm, "radius": 1.05 * mm});
            skSolve(sketch);
        }
        {
            var Q0;
            Q0=makeQuery(id+"F20.imprint","IMPRINT",FACE,{"disambiguationData":[TD([[makeQuery(id+"F20.imprint","IMPRINT",EDGE,{"derivedFrom":sQuery(id+"F20.wireOp",EDGE,"E71")}),1.0]])]});
            var Q1;
            Q1=makeQuery(id+"F20.imprint","IMPRINT",FACE,{"disambiguationData":[TD([[makeQuery(id+"F20.imprint","IMPRINT",EDGE,{"derivedFrom":sQuery(id+"F20.wireOp",EDGE,"E73")}),1.0]])]});
            var Q2;
            Q2=makeQuery(id+"F20.imprint","IMPRINT",FACE,{"disambiguationData":[TD([[makeQuery(id+"F20.imprint","IMPRINT",EDGE,{"derivedFrom":sQuery(id+"F20.wireOp",EDGE,"E75")}),1.0]])]});
            var Q3;
            Q3=makeQuery(id+"F20.imprint","IMPRINT",FACE,{"disambiguationData":[TD([[makeQuery(id+"F20.imprint","IMPRINT",EDGE,{"derivedFrom":sQuery(id+"F20.wireOp",EDGE,"E74")}),1.0]])]});
            var Q4;
            Q4=makeQuery(id+"F20.imprint","IMPRINT",FACE,{"disambiguationData":[TD([[makeQuery(id+"F20.imprint","IMPRINT",EDGE,{"derivedFrom":sQuery(id+"F20.wireOp",EDGE,"E72")}),1.0]])]});
            var Q5;
            Q5=makeQuery(id+"F20.imprint","IMPRINT",FACE,{"disambiguationData":[TD([[makeQuery(id+"F20.imprint","IMPRINT",EDGE,{"derivedFrom":sQuery(id+"F20.wireOp",EDGE,"E79.bottom")}),1.0]])]});
            var Q6;
            Q6=makeQuery(id+"F20.imprint","IMPRINT",FACE,{"disambiguationData":[TD([[makeQuery(id+"F20.imprint","IMPRINT",EDGE,{"derivedFrom":sQuery(id+"F20.wireOp",EDGE,"E76")}),1.0]])]});
            var Q7;
            Q7=makeQuery(id+"F20.imprint","IMPRINT",FACE,{"disambiguationData":[TD([[makeQuery(id+"F20.imprint","IMPRINT",EDGE,{"derivedFrom":sQuery(id+"F20.wireOp",EDGE,"E78.bottom")}),1.0]])]});
            var Q8;
            Q8=makeQuery(id+"F20.imprint","IMPRINT",FACE,{"disambiguationData":[TD([[makeQuery(id+"F20.imprint","IMPRINT",EDGE,{"derivedFrom":sQuery(id+"F20.wireOp",EDGE,"E77")}),1.0]])]});
            var Q9;
            Q9=makeQuery(id+"F20.imprint","IMPRINT",FACE,{"disambiguationData":[TD([[makeQuery(id+"F20.imprint","IMPRINT",EDGE,{"derivedFrom":sQuery(id+"F20.wireOp",EDGE,"E83")}),1.0]])]});
            var Q10;
            Q10=makeQuery(id+"F20.imprint","IMPRINT",FACE,{"disambiguationData":[TD([[makeQuery(id+"F20.imprint","IMPRINT",EDGE,{"derivedFrom":sQuery(id+"F20.wireOp",EDGE,"E82")}),1.0]])]});
            var Q11;
            Q11=makeQuery(id+"F20.imprint","IMPRINT",FACE,{"disambiguationData":[TD([[makeQuery(id+"F20.imprint","IMPRINT",EDGE,{"derivedFrom":sQuery(id+"F20.wireOp",EDGE,"E80")}),1.0]])]});
            var Q12;
            Q12=makeQuery(id+"F20.imprint","IMPRINT",FACE,{"disambiguationData":[TD([[makeQuery(id+"F20.imprint","IMPRINT",EDGE,{"derivedFrom":sQuery(id+"F20.wireOp",EDGE,"E81")}),1.0]])]});
            var Q13;
            Q13=makeQuery(id+"F20.imprint","IMPRINT",FACE,{"disambiguationData":[TD([[makeQuery(id+"F20.imprint","IMPRINT",EDGE,{"derivedFrom":sQuery(id+"F20.wireOp",EDGE,"E91")}),1.0]])]});
            var Q14;
            Q14=makeQuery(id+"F20.imprint","IMPRINT",FACE,{"disambiguationData":[TD([[makeQuery(id+"F20.imprint","IMPRINT",EDGE,{"derivedFrom":sQuery(id+"F20.wireOp",EDGE,"E92")}),1.0]])]});
            var Q15;
            Q15=makeQuery(id+"F20.imprint","IMPRINT",FACE,{"disambiguationData":[TD([[makeQuery(id+"F20.imprint","IMPRINT",EDGE,{"derivedFrom":sQuery(id+"F20.wireOp",EDGE,"E84")}),1.0]])]});
            var Q16;
            Q16=makeQuery(id+"F20.imprint","IMPRINT",FACE,{"disambiguationData":[TD([[makeQuery(id+"F20.imprint","IMPRINT",EDGE,{"derivedFrom":sQuery(id+"F20.wireOp",EDGE,"E85")}),1.0]])]});
            var Q17;
            Q17=makeQuery(id+"F20.imprint","IMPRINT",FACE,{"disambiguationData":[TD([[makeQuery(id+"F20.imprint","IMPRINT",EDGE,{"derivedFrom":sQuery(id+"F20.wireOp",EDGE,"E86")}),1.0]])]});
            var Q18;
            Q18=makeQuery(id+"F20.imprint","IMPRINT",FACE,{"disambiguationData":[TD([[makeQuery(id+"F20.imprint","IMPRINT",EDGE,{"derivedFrom":sQuery(id+"F20.wireOp",EDGE,"E87")}),1.0]])]});
            var Q19;
            Q19=makeQuery(id+"F20.imprint","IMPRINT",FACE,{"disambiguationData":[TD([[makeQuery(id+"F20.imprint","IMPRINT",EDGE,{"derivedFrom":sQuery(id+"F20.wireOp",EDGE,"E88")}),1.0]])]});
            var Q20;
            Q20=makeQuery(id+"F20.imprint","IMPRINT",FACE,{"disambiguationData":[TD([[makeQuery(id+"F20.imprint","IMPRINT",EDGE,{"derivedFrom":sQuery(id+"F20.wireOp",EDGE,"E93")}),1.0]])]});
            var Q21;
            Q21=makeQuery(id+"F20.imprint","IMPRINT",FACE,{"disambiguationData":[TD([[makeQuery(id+"F20.imprint","IMPRINT",EDGE,{"derivedFrom":sQuery(id+"F20.wireOp",EDGE,"E89")}),1.0]])]});
            var Q22;
            Q22=makeQuery(id+"F20.imprint","IMPRINT",FACE,{"disambiguationData":[TD([[makeQuery(id+"F20.imprint","IMPRINT",EDGE,{"derivedFrom":sQuery(id+"F20.wireOp",EDGE,"E90")}),1.0]])]});
            extrude(context, id + "F21", {"entities" : qUnion([Q0, Q1, Q2, Q3, Q4, Q5, Q6, Q7, Q8, Q9, Q10, Q11, Q12, Q13, Q14, Q15, Q16, Q17, Q18, Q19, Q20, Q21, Q22]), "operationType" : NewBodyOperationType.REMOVE, "oppositeDirection" : true, "depth" : 2 * mm, "offsetDistance" : 25 * mm});
        }
    });
